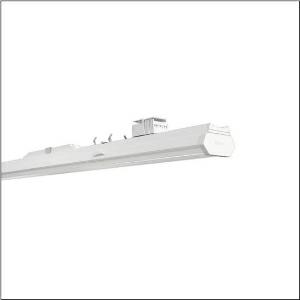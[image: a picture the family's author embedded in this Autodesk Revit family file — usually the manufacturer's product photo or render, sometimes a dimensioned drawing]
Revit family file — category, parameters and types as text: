
# Revit family: licross_r__11_protected_ho_51tp13dn4f5s_0b0f
name_source: partatom
category: Lighting Fixtures
units: mm (PartAtom-declared; Revit-internal decimal feet)

## family parameters
Cut with Voids When Loaded = No
Host = Face
Light Source = No
Part Type = Normal
Room Calculation Point = No
Round Connector Dimension = Use Diameter
Shared = No

## types (1)
- --- (1 x LED, 15550 lm, 87.3 W, 4000K)
    Apparent Load = 87 VA
    CIE Flux Codes = 89 96 99 100 99
    Color Rendering = 80
    Color Temperature = 4000K
    Default Elevation = 1800 mm
    Description = Licross® 11 Protected HO, luminaire insert, of sheet steel, galvanised, coil coated, white, length: 1.500mm, width: 90mm, height: 101mm, LED rated luminous flux: 15.550lm, light colour: 840, control gear: DALI 2, with plug, 5-pole, with phase selection, mains connection: 220..240V, AC, 50/60Hz, rated input power: 87W, internal wiring halogen-free, primary light control with lens, of plastic, primary optical cover: cover, of PMMA, light emission: direct distribution, primary light characteristic: symmetric, protection rating (complete): IP64, insulation class (complete): insulation class I (protective earthing), certification: CE, ENEC, VDE, UKCA, protection symbol: D if used in an environment with conductive dust loads with corresponding accessories, impact resistance: IK06, permissible ambient temperature for indoor applications: -25..+30°C, corresponds to IFS (International Featured Standards) requirements for safety and quality in the food industry, reducing of maximum allowable ambient temperature of 5°C with ceiling mounting, LABS conformity tested according to VDMA 24364:2018-05, packaging unit: 1 piece
    Height = 92 mm
    Lamp = 1 x LED
    Lamp Light Flux = 15550 lm
    Lamp Power = 87.3 W
    Lamp count = 1
    Length = 1500 mm
    Luminous efficacy = 178 lm/W
    Manufacturer = Siteco
    ModVariant = No
    Model = 51TP13DN4F5S
    Mounting Place = Ceiling
    Mounting Type = Pendant
    Number of Poles = 1
    OnlyDefault = Yes
    Power Factor = 1
    Product Name = Licross® 11 Protected HO
    Product group = luminaire insert | ceiling pendant
    ProductGroupID = 902
    Protection Class = Protection class I
    Protection Degree = IP 64
    RLX_Detail_Level = 1
    RLX_Emergency_Light_Flux = 0 lm
    RLX_Emergency_Type = 0
    RLX_Emergency_Type_DB = No
    RlxData = <blob elided: 24337 chars, md5=f6d30915>
    Socket = socket
    Standby Power = 0 W
    System Light Flux = 15550 lm
    System Power = 87 W
    Type Comments = factory setting: luminous flux: 100 % | dim-lin: 254 | 589 mA
    Type Image = l_1256148.jpg
    URL = http://relux.com
    VarID = @adj_122281
    Voltage = 0 V
    Weight = 0.00 kg
    Width = 88 mm

## geometry (parser evidence)
native form markers: Blend x4, Sweep x12
no freeform markers — native parametric forms only
